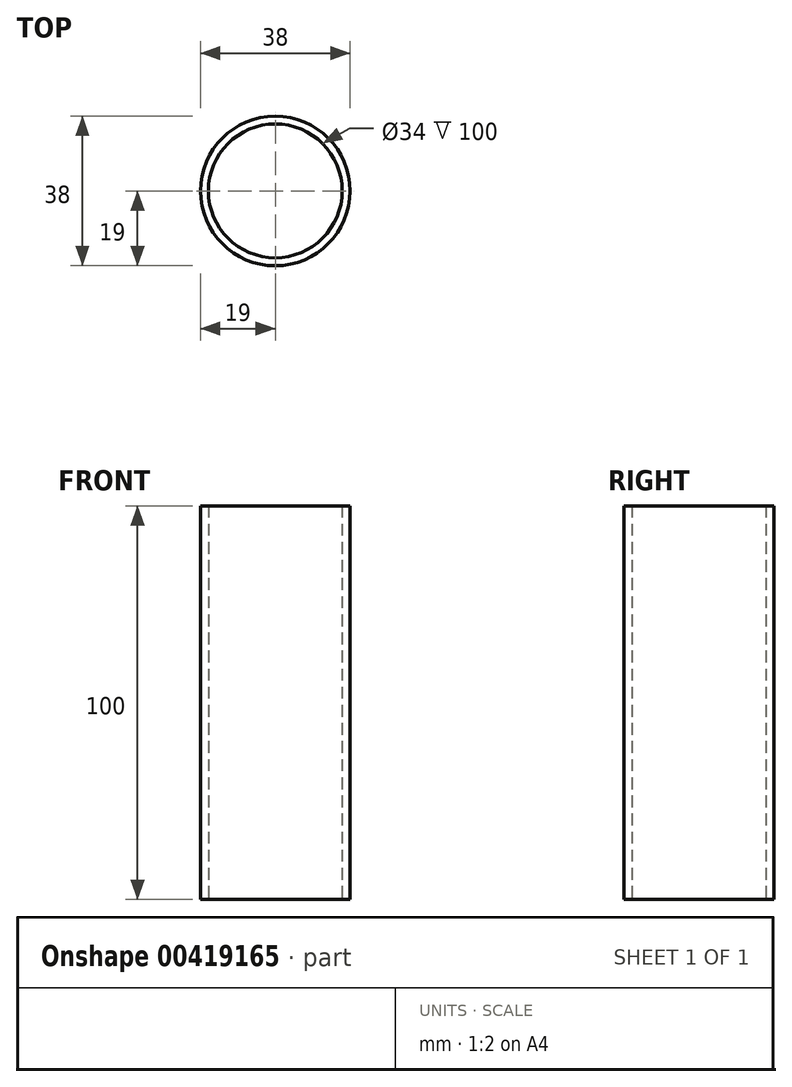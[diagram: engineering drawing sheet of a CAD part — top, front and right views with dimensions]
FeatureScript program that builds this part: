
annotation { "Feature Type Name" : "Feature", "Feature Type Description" : "" }
export const myFeature = defineFeature(function(context is Context, id is Id, definition is map)
    precondition{}
    {
        {
            var Q0;
            Q0=qCreatedBy(makeId("Top.planeOp"),FACE);
            var sketch = newSketch(context, id + "F0", { "sketchPlane" : qUnion([Q0])});
            skCircle(sketch, "E0", {"center": v(0, 0) * mm, "radius": 19 * mm});
            skCircle(sketch, "E1", {"center": v(0, 0) * mm, "radius": 17 * mm});
            skSolve(sketch);
        }
        {
            var Q0;
            Q0 = qSketchRegion(id + "F0", true);
            extrude(context, id + "F1", {"entities" : qUnion([Q0]), "depth" : 100 * mm});
        }
    });
